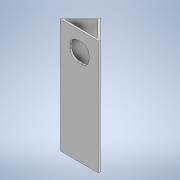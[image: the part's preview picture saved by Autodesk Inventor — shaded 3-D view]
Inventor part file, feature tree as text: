
AUTODESK INVENTOR PART (.ipt)
format: ipt  version: 2020 (Build 240168000, 168)  size: 142,848 bytes
history: native  units: mm
features: extrude x3, sketch x3
ambient origin geometry x8: Origin, YZ Plane, XZ Plane, XY Plane, X Axis, Y Axis, Z Axis, Center Point
bodies: Solid1 (feature_tree)
feature tree (6):
  extrude  "Extrusion1"  Depth=300.0mm
  extrude  "Extrusion2"  TaperAngle=45.0deg  [1 undecoded]
  extrude  "Extrusion7"  Depth=5.0mm
  sketch  "Sketch1"  dims[d0=100.0mm d1=300.0mm]
  sketch  "Sketch2"  dims[d2=5.0mm d3=0.0mm d4=45.0deg]
  sketch  "Sketch7"  dims[d5=5.0mm d6=5.0mm d7=150.0mm d8=0.0mm d26=50.0mm d27=50.0mm d28=20.0mm d29=5.0mm d30=0.0mm]
note: 1 required parameter value undecoded (feature->parameter linkage not recoverable at this tier; creation-order binding heuristic only, values carry confidence <= 0.55)
